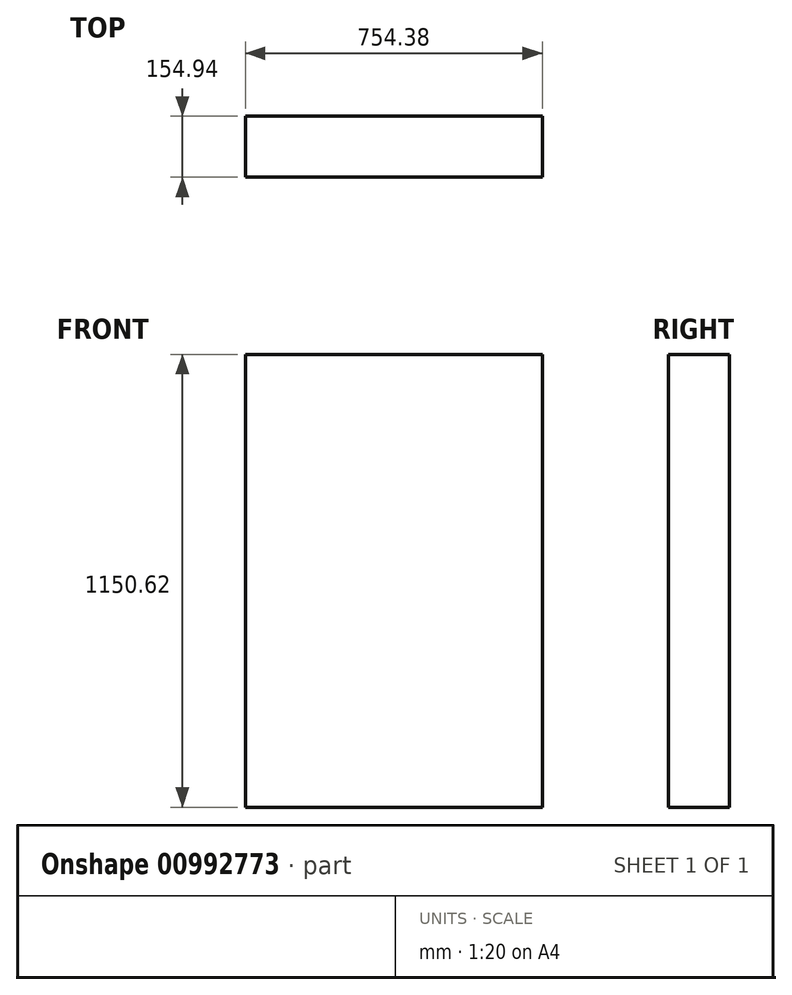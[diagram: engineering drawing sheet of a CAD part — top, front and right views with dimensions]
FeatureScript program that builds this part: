
annotation { "Feature Type Name" : "Feature", "Feature Type Description" : "" }
export const myFeature = defineFeature(function(context is Context, id is Id, definition is map)
    precondition{}
    {
        {
            var Q0;
            Q0=qCreatedBy(makeId("Top.planeOp"),FACE);
            var sketch = newSketch(context, id + "F0", { "sketchPlane" : qUnion([Q0])});
            skLineSegment(sketch, "E0.bottom", {"start": v(377.2, -77.47) * mm, "end": v(-377.2, -77.47) * mm});
            skLineSegment(sketch, "E0.top", {"start": v(377.2, 77.47) * mm, "end": v(-377.2, 77.47) * mm});
            skLineSegment(sketch, "E0.left", {"start": v(377.2, -77.47) * mm, "end": v(377.2, 77.47) * mm});
            skLineSegment(sketch, "E0.right", {"start": v(-377.2, -77.47) * mm, "end": v(-377.2, 77.47) * mm});
            skPoint(sketch, "E0.middle", {"position": v(0, 0) * mm});
            skSolve(sketch);
        }
        {
            var Q0;
            Q0 = qSketchRegion(id + "F0", true);
            extrude(context, id + "F1", {"entities" : qUnion([Q0]), "depth" : 1150.62 * mm, "offsetDistance" : 25.4 * mm});
        }
    });
